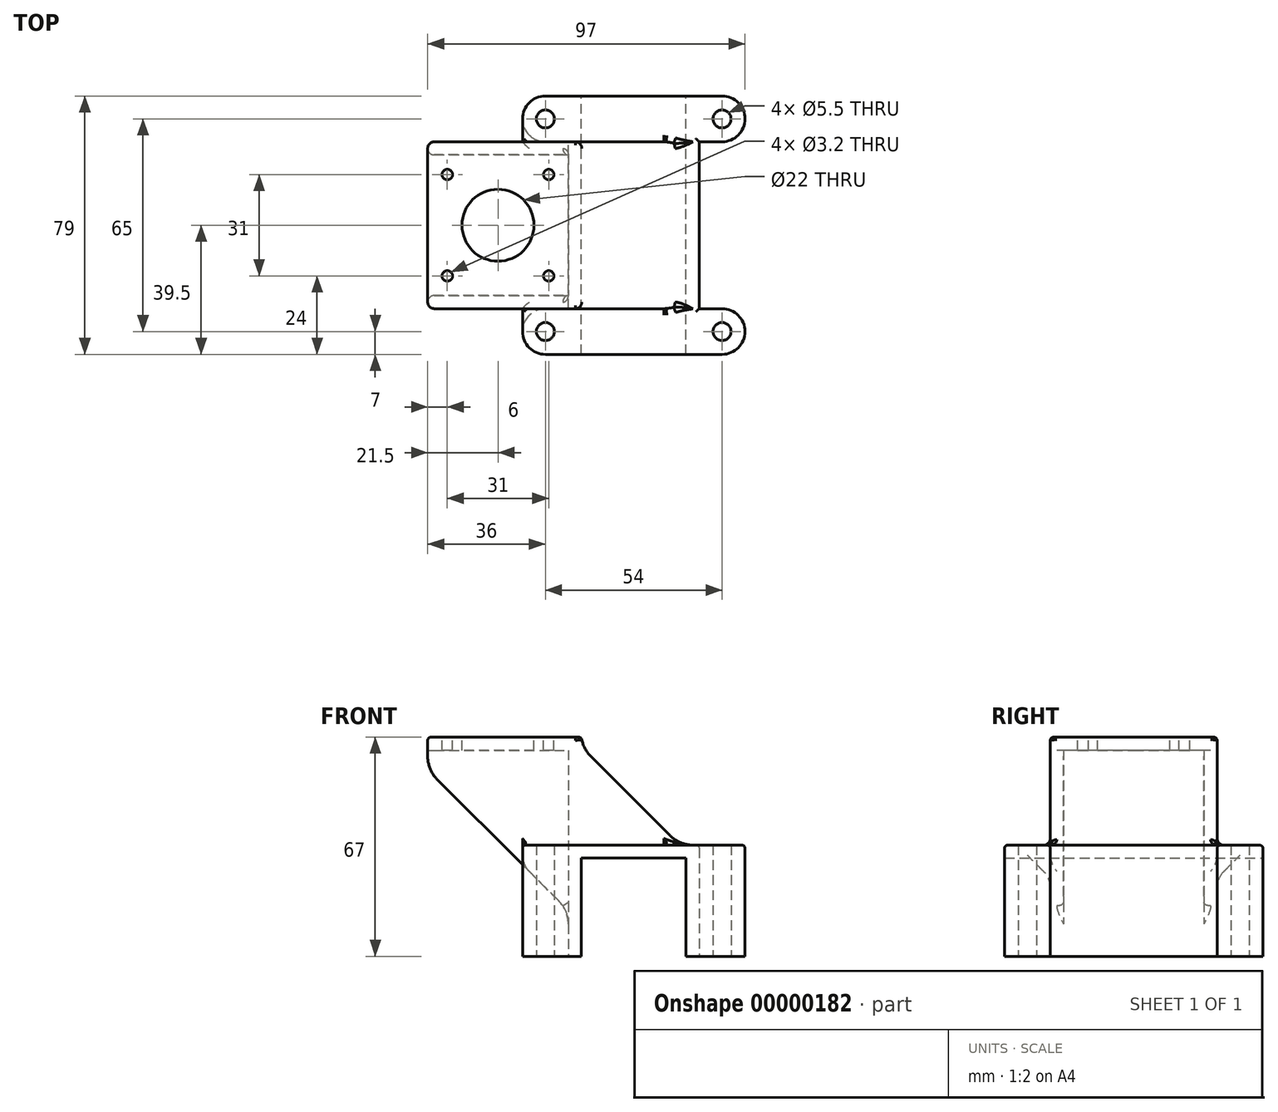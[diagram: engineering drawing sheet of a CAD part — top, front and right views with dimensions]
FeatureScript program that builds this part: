
annotation { "Feature Type Name" : "Feature", "Feature Type Description" : "" }
export const myFeature = defineFeature(function(context is Context, id is Id, definition is map)
    precondition{}
    {
        {
            var Q0;
            Q0=qCreatedBy(makeId("Front.planeOp"),FACE);
            var sketch = newSketch(context, id + "F0", { "sketchPlane" : qUnion([Q0])});
            skLineSegment(sketch, "E0.bottom", {"start": v(-20, 20) * mm, "end": v(20, 20) * mm});
            skLineSegment(sketch, "E0.top", {"start": v(-20, 0) * mm, "end": v(20, 0) * mm, "construction": true});
            skLineSegment(sketch, "E0.left", {"start": v(-20, 20) * mm, "end": v(-20, 0) * mm});
            skLineSegment(sketch, "E0.right", {"start": v(20, 20) * mm, "end": v(20, 0) * mm});
            skLineSegment(sketch, "E1.bottom", {"start": v(-16, 0) * mm, "end": v(16, 0) * mm, "construction": true});
            skLineSegment(sketch, "E1.top", {"start": v(-16, 16) * mm, "end": v(16, 16) * mm});
            skLineSegment(sketch, "E1.left", {"start": v(-16, 0) * mm, "end": v(-16, 16) * mm});
            skLineSegment(sketch, "E1.right", {"start": v(16, 0) * mm, "end": v(16, 16) * mm});
            skLineSegment(sketch, "E2", {"start": v(-20, 0) * mm, "end": v(-16, 0) * mm});
            skLineSegment(sketch, "E3", {"start": v(16, 0) * mm, "end": v(20, 0) * mm});
            skSolve(sketch);
        }
        {
            var Q0;
            Q0=makeQuery(id+"F0.imprint","IMPRINT",FACE,{"disambiguationData":[TD([[makeQuery(id+"F0.imprint","IMPRINT",EDGE,{"derivedFrom":sQuery(id+"F0.wireOp",EDGE,"E0.bottom")}),-1.0]])]});
            extrude(context, id + "F1", {"entities" : qUnion([Q0]), "depth" : 79 * mm});
        }
        {
            var Q0;
            Q0=qCreatedBy(makeId("Top.planeOp"),FACE);
            var sketch = newSketch(context, id + "F2", { "sketchPlane" : qUnion([Q0])});
            skCircle(sketch, "E4", {"center": v(-27, -7) * mm, "radius": 7 * mm, "construction": true});
            skCircle(sketch, "E5", {"center": v(-27, -72) * mm, "radius": 7 * mm, "construction": true});
            skCircle(sketch, "E6", {"center": v(27, -7) * mm, "radius": 7 * mm, "construction": true});
            skCircle(sketch, "E7", {"center": v(27, -72) * mm, "radius": 7 * mm, "construction": true});
            skLineSegment(sketch, "E8.bottom", {"start": v(-27, 0) * mm, "end": v(-20, 0) * mm});
            skLineSegment(sketch, "E8.top", {"start": v(-27, -14) * mm, "end": v(-20, -14) * mm});
            skLineSegment(sketch, "E8.left", {"start": v(-27, 0) * mm, "end": v(-27, -14) * mm});
            skLineSegment(sketch, "E8.right", {"start": v(-20, 0) * mm, "end": v(-20, -14) * mm});
            skLineSegment(sketch, "E9.bottom", {"start": v(27, 0) * mm, "end": v(20, 0) * mm});
            skLineSegment(sketch, "E9.top", {"start": v(27, -14) * mm, "end": v(20, -14) * mm});
            skLineSegment(sketch, "E9.left", {"start": v(27, 0) * mm, "end": v(27, -14) * mm});
            skLineSegment(sketch, "E9.right", {"start": v(20, 0) * mm, "end": v(20, -14) * mm});
            skLineSegment(sketch, "E10.bottom", {"start": v(-27, -65) * mm, "end": v(-20, -65) * mm});
            skLineSegment(sketch, "E10.top", {"start": v(-27, -79) * mm, "end": v(-20, -79) * mm});
            skLineSegment(sketch, "E10.left", {"start": v(-27, -65) * mm, "end": v(-27, -79) * mm});
            skLineSegment(sketch, "E10.right", {"start": v(-20, -65) * mm, "end": v(-20, -79) * mm});
            skLineSegment(sketch, "E11.bottom", {"start": v(27, -65) * mm, "end": v(20, -65) * mm});
            skLineSegment(sketch, "E11.top", {"start": v(27, -79) * mm, "end": v(20, -79) * mm});
            skLineSegment(sketch, "E11.left", {"start": v(27, -65) * mm, "end": v(27, -79) * mm});
            skLineSegment(sketch, "E11.right", {"start": v(20, -65) * mm, "end": v(20, -79) * mm});
            skLineSegment(sketch, "E12.bottom", {"start": v(-27, 0) * mm, "end": v(-34, 0) * mm});
            skLineSegment(sketch, "E12.top", {"start": v(-27, -14) * mm, "end": v(-34, -14) * mm});
            skLineSegment(sketch, "E12.right", {"start": v(-34, 0) * mm, "end": v(-34, -14) * mm});
            skLineSegment(sketch, "E13.bottom", {"start": v(-27, -65) * mm, "end": v(-34, -65) * mm});
            skLineSegment(sketch, "E13.top", {"start": v(-27, -79) * mm, "end": v(-34, -79) * mm});
            skLineSegment(sketch, "E13.right", {"start": v(-34, -65) * mm, "end": v(-34, -79) * mm});
            skLineSegment(sketch, "E14.bottom", {"start": v(27, 0) * mm, "end": v(34, 0) * mm});
            skLineSegment(sketch, "E14.top", {"start": v(27, -14) * mm, "end": v(34, -14) * mm});
            skLineSegment(sketch, "E14.right", {"start": v(34, 0) * mm, "end": v(34, -14) * mm});
            skLineSegment(sketch, "E15.bottom", {"start": v(27, -65) * mm, "end": v(34, -65) * mm});
            skLineSegment(sketch, "E15.top", {"start": v(27, -79) * mm, "end": v(34, -79) * mm});
            skLineSegment(sketch, "E15.right", {"start": v(34, -65) * mm, "end": v(34, -79) * mm});
            skSolve(sketch);
        }
        {
            var Q0;
            {Q0=qUnion([makeQuery(id+"F2.imprint","IMPRINT",FACE,{"disambiguationData":[TD([[makeQuery(id+"F2.imprint","IMPRINT",EDGE,{"derivedFrom":sQuery(id+"F2.wireOp",EDGE,"E8.bottom")}),-1.0]])]}),makeQuery(id+"F2.imprint","IMPRINT",FACE,{"disambiguationData":[TD([[makeQuery(id+"F2.imprint","IMPRINT",EDGE,{"derivedFrom":sQuery(id+"F2.wireOp",EDGE,"E12.bottom")}),1.0]])]}),makeQuery(id+"F2.imprint","IMPRINT",FACE,{"disambiguationData":[TD([[makeQuery(id+"F2.imprint","IMPRINT",EDGE,{"derivedFrom":sQuery(id+"F2.wireOp",EDGE,"E9.bottom")}),1.0]])]}),makeQuery(id+"F2.imprint","IMPRINT",FACE,{"disambiguationData":[TD([[makeQuery(id+"F2.imprint","IMPRINT",EDGE,{"derivedFrom":sQuery(id+"F2.wireOp",EDGE,"E14.bottom")}),-1.0]])]}),makeQuery(id+"F2.imprint","IMPRINT",FACE,{"disambiguationData":[TD([[makeQuery(id+"F2.imprint","IMPRINT",EDGE,{"derivedFrom":sQuery(id+"F2.wireOp",EDGE,"E10.bottom")}),-1.0]])]}),makeQuery(id+"F2.imprint","IMPRINT",FACE,{"disambiguationData":[TD([[makeQuery(id+"F2.imprint","IMPRINT",EDGE,{"derivedFrom":sQuery(id+"F2.wireOp",EDGE,"E13.bottom")}),1.0]])]}),makeQuery(id+"F2.imprint","IMPRINT",FACE,{"disambiguationData":[TD([[makeQuery(id+"F2.imprint","IMPRINT",EDGE,{"derivedFrom":sQuery(id+"F2.wireOp",EDGE,"E11.bottom")}),1.0]])]}),makeQuery(id+"F2.imprint","IMPRINT",FACE,{"disambiguationData":[TD([[makeQuery(id+"F2.imprint","IMPRINT",EDGE,{"derivedFrom":sQuery(id+"F2.wireOp",EDGE,"E15.bottom")}),-1.0]])]})]);}
            var Q1;
            Q1=makeQuery(id+"F1.opExtrude","SWEPT_FACE",FACE,{"disambiguationData":[OSD([sQuery(id+"F0.wireOp",EDGE,"E0.bottom")])]});
            extrude(context, id + "F3", {"entities" : qUnion([Q0]), "operationType" : NewBodyOperationType.ADD, "endBound" : BoundingType.UP_TO_SURFACE, "endBoundEntityFace" : qUnion([Q1]), "depth" : 25 * mm});
        }
        {
            var Q0;
            Q0=qCreatedBy(makeId("Top.planeOp"),FACE);
            var sketch = newSketch(context, id + "F4", { "sketchPlane" : qUnion([Q0])});
            skCircle(sketch, "E16", {"center": v(-27, -7) * mm, "radius": 2.75 * mm});
            skCircle(sketch, "E17", {"center": v(27, -7) * mm, "radius": 2.75 * mm});
            skCircle(sketch, "E18", {"center": v(27, -72) * mm, "radius": 2.75 * mm});
            skCircle(sketch, "E19", {"center": v(-27, -72) * mm, "radius": 2.75 * mm});
            skLineSegment(sketch, "E20.bottom", {"start": v(-27, -7) * mm, "end": v(27, -7) * mm, "construction": true});
            skLineSegment(sketch, "E20.top", {"start": v(-27, -72) * mm, "end": v(27, -72) * mm, "construction": true});
            skLineSegment(sketch, "E20.left", {"start": v(-27, -7) * mm, "end": v(-27, -72) * mm, "construction": true});
            skLineSegment(sketch, "E20.right", {"start": v(27, -7) * mm, "end": v(27, -72) * mm, "construction": true});
            skSolve(sketch);
        }
        {
            var Q0;
            {Q0=qUnion([makeQuery(id+"F4.imprint","IMPRINT",FACE,{"disambiguationData":[TD([[makeQuery(id+"F4.imprint","IMPRINT",EDGE,{"derivedFrom":sQuery(id+"F4.wireOp",EDGE,"E16")}),1.0]])]}),makeQuery(id+"F4.imprint","IMPRINT",FACE,{"disambiguationData":[TD([[makeQuery(id+"F4.imprint","IMPRINT",EDGE,{"derivedFrom":sQuery(id+"F4.wireOp",EDGE,"E17")}),1.0]])]}),makeQuery(id+"F4.imprint","IMPRINT",FACE,{"disambiguationData":[TD([[makeQuery(id+"F4.imprint","IMPRINT",EDGE,{"derivedFrom":sQuery(id+"F4.wireOp",EDGE,"E18")}),1.0]])]}),makeQuery(id+"F4.imprint","IMPRINT",FACE,{"disambiguationData":[TD([[makeQuery(id+"F4.imprint","IMPRINT",EDGE,{"derivedFrom":sQuery(id+"F4.wireOp",EDGE,"E19")}),1.0]])]})]);}
            var Q1;
            Q1=makeQuery(id+"F3.boolean.opBoolean","MERGE",FACE,{"derivedFrom":[makeQuery(id+"F1.opExtrude","SWEPT_FACE",FACE,{"disambiguationData":[OSD([sQuery(id+"F0.wireOp",EDGE,"E0.bottom")])]}),makeQuery(id+"F3.opExtrude","CAP_FACE",FACE,{"disambiguationData":[OSD([sQuery(id+"F2.wireOp",EDGE,"E8.bottom"),sQuery(id+"F2.wireOp",EDGE,"E8.top"),sQuery(id+"F2.wireOp",EDGE,"E8.right"),sQuery(id+"F2.wireOp",EDGE,"E12.bottom"),sQuery(id+"F2.wireOp",EDGE,"E12.top"),sQuery(id+"F2.wireOp",EDGE,"E12.right")])],"isStart":false}),makeQuery(id+"F3.opExtrude","CAP_FACE",FACE,{"disambiguationData":[OSD([sQuery(id+"F2.wireOp",EDGE,"E9.bottom"),sQuery(id+"F2.wireOp",EDGE,"E9.top"),sQuery(id+"F2.wireOp",EDGE,"E9.right"),sQuery(id+"F2.wireOp",EDGE,"E14.bottom"),sQuery(id+"F2.wireOp",EDGE,"E14.top"),sQuery(id+"F2.wireOp",EDGE,"E14.right")])],"isStart":false}),makeQuery(id+"F3.opExtrude","CAP_FACE",FACE,{"disambiguationData":[OSD([sQuery(id+"F2.wireOp",EDGE,"E10.bottom"),sQuery(id+"F2.wireOp",EDGE,"E10.top"),sQuery(id+"F2.wireOp",EDGE,"E10.right"),sQuery(id+"F2.wireOp",EDGE,"E13.bottom"),sQuery(id+"F2.wireOp",EDGE,"E13.top"),sQuery(id+"F2.wireOp",EDGE,"E13.right")])],"isStart":false}),makeQuery(id+"F3.opExtrude","CAP_FACE",FACE,{"disambiguationData":[OSD([sQuery(id+"F2.wireOp",EDGE,"E11.bottom"),sQuery(id+"F2.wireOp",EDGE,"E11.top"),sQuery(id+"F2.wireOp",EDGE,"E11.right"),sQuery(id+"F2.wireOp",EDGE,"E15.bottom"),sQuery(id+"F2.wireOp",EDGE,"E15.top"),sQuery(id+"F2.wireOp",EDGE,"E15.right")])],"isStart":false})]});
            extrude(context, id + "F5", {"entities" : qUnion([Q0]), "operationType" : NewBodyOperationType.REMOVE, "endBound" : BoundingType.UP_TO_SURFACE, "endBoundEntityFace" : qUnion([Q1]), "depth" : 25 * mm});
        }
        {
            var Q0;
            Q0=makeQuery(id+"F3.boolean.opBoolean","MERGE",FACE,{"derivedFrom":[makeQuery(id+"F1.opExtrude","SWEPT_FACE",FACE,{"disambiguationData":[OSD([sQuery(id+"F0.wireOp",EDGE,"E2")])]}),makeQuery(id+"F3.opExtrude","CAP_FACE",FACE,{"disambiguationData":[OSD([sQuery(id+"F2.wireOp",EDGE,"E8.bottom"),sQuery(id+"F2.wireOp",EDGE,"E8.top"),sQuery(id+"F2.wireOp",EDGE,"E8.right"),sQuery(id+"F2.wireOp",EDGE,"E12.bottom"),sQuery(id+"F2.wireOp",EDGE,"E12.top"),sQuery(id+"F2.wireOp",EDGE,"E12.right")])],"isStart":true}),makeQuery(id+"F3.opExtrude","CAP_FACE",FACE,{"disambiguationData":[OSD([sQuery(id+"F2.wireOp",EDGE,"E10.bottom"),sQuery(id+"F2.wireOp",EDGE,"E10.top"),sQuery(id+"F2.wireOp",EDGE,"E10.right"),sQuery(id+"F2.wireOp",EDGE,"E13.bottom"),sQuery(id+"F2.wireOp",EDGE,"E13.top"),sQuery(id+"F2.wireOp",EDGE,"E13.right")])],"isStart":true})]});
            var Q1;
            Q1=makeQuery(id+"F3.boolean.opBoolean","MERGE",FACE,{"derivedFrom":[makeQuery(id+"F1.opExtrude","SWEPT_FACE",FACE,{"disambiguationData":[OSD([sQuery(id+"F0.wireOp",EDGE,"E3")])]}),makeQuery(id+"F3.opExtrude","CAP_FACE",FACE,{"disambiguationData":[OSD([sQuery(id+"F2.wireOp",EDGE,"E9.bottom"),sQuery(id+"F2.wireOp",EDGE,"E9.top"),sQuery(id+"F2.wireOp",EDGE,"E9.right"),sQuery(id+"F2.wireOp",EDGE,"E14.bottom"),sQuery(id+"F2.wireOp",EDGE,"E14.top"),sQuery(id+"F2.wireOp",EDGE,"E14.right")])],"isStart":true}),makeQuery(id+"F3.opExtrude","CAP_FACE",FACE,{"disambiguationData":[OSD([sQuery(id+"F2.wireOp",EDGE,"E11.bottom"),sQuery(id+"F2.wireOp",EDGE,"E11.top"),sQuery(id+"F2.wireOp",EDGE,"E11.right"),sQuery(id+"F2.wireOp",EDGE,"E15.bottom"),sQuery(id+"F2.wireOp",EDGE,"E15.top"),sQuery(id+"F2.wireOp",EDGE,"E15.right")])],"isStart":true})]});
            extrude(context, id + "F6", {"entities" : qUnion([Q0, Q1]), "operationType" : NewBodyOperationType.ADD, "depth" : 14 * mm});
        }
        {
            var Q0;
            Q0=qCreatedBy(makeId("Top.planeOp"),FACE);
            var sketch = newSketch(context, id + "F7", { "sketchPlane" : qUnion([Q0])});
            skLineSegment(sketch, "E21.bottom", {"start": v(-63, -14) * mm, "end": v(-16, -14) * mm});
            skLineSegment(sketch, "E21.top", {"start": v(-63, -65) * mm, "end": v(-16, -65) * mm});
            skLineSegment(sketch, "E21.left", {"start": v(-63, -14) * mm, "end": v(-63, -65) * mm});
            skLineSegment(sketch, "E21.right", {"start": v(-16, -14) * mm, "end": v(-16, -65) * mm});
            skLineSegment(sketch, "E22", {"start": v(-63, -39.5) * mm, "end": v(20, -39.5) * mm, "construction": true});
            skSolve(sketch);
        }
        {
            var Q0;
            Q0=makeQuery(id+"F7.imprint","IMPRINT",FACE,{"disambiguationData":[TD([[makeQuery(id+"F7.imprint","IMPRINT",EDGE,{"derivedFrom":sQuery(id+"F7.wireOp",EDGE,"E21.bottom")}),-1.0]])]});
            var Q1;
            Q1=makeQuery(id+"F1.opExtrude","SWEPT_FACE",FACE,{"disambiguationData":[OSD([sQuery(id+"F0.wireOp",EDGE,"E1.top")])]});
            extrude(context, id + "F8", {"entities" : qUnion([Q0]), "operationType" : NewBodyOperationType.ADD, "endBoundEntity" : qUnion([Q1]), "depth" : 53 * mm});
        }
        {
            var Q0;
            Q0=makeQuery(id+"F8.opExtrude","CAP_EDGE",EDGE,{"disambiguationData":[OSD([sQuery(id+"F7.wireOp",EDGE,"E21.left")])],"isStart":true});
            chamfer(context, id + "F9", {"entities" : qUnion([Q0]), "width" : 43 * mm, "tangentPropagation" : true});
        }
        {
            var Q0;
            Q0=qCreatedBy(makeId("Top.planeOp"),FACE);
            var sketch = newSketch(context, id + "F10", { "sketchPlane" : qUnion([Q0])});
            skLineSegment(sketch, "E23.bottom", {"start": v(-63, -18) * mm, "end": v(-20, -18) * mm});
            skLineSegment(sketch, "E23.top", {"start": v(-63, -61) * mm, "end": v(-20, -61) * mm});
            skLineSegment(sketch, "E23.left", {"start": v(-63, -18) * mm, "end": v(-63, -61) * mm});
            skLineSegment(sketch, "E23.right", {"start": v(-20, -18) * mm, "end": v(-20, -61) * mm});
            skLineSegment(sketch, "E24", {"start": v(-63, -39.5) * mm, "end": v(-20, -39.5) * mm, "construction": true});
            skSolve(sketch);
        }
        {
            var Q0;
            Q0=makeQuery(id+"F10.imprint","IMPRINT",FACE,{"disambiguationData":[TD([[makeQuery(id+"F10.imprint","IMPRINT",EDGE,{"derivedFrom":sQuery(id+"F10.wireOp",EDGE,"E23.bottom")}),-1.0]])]});
            extrude(context, id + "F11", {"entities" : qUnion([Q0]), "operationType" : NewBodyOperationType.REMOVE, "depth" : 49 * mm});
        }
        {
            var Q0;
            Q0=makeQuery(id+"F8.boolean.opBoolean","INTERSECT",EDGE,{"derivedFrom":[makeQuery(id+"F3.boolean.opBoolean","MERGE",FACE,{"derivedFrom":[makeQuery(id+"F1.opExtrude","SWEPT_FACE",FACE,{"disambiguationData":[OSD([sQuery(id+"F0.wireOp",EDGE,"E0.bottom")])]}),makeQuery(id+"F3.opExtrude","CAP_FACE",FACE,{"disambiguationData":[OSD([sQuery(id+"F2.wireOp",EDGE,"E8.bottom"),sQuery(id+"F2.wireOp",EDGE,"E8.top"),sQuery(id+"F2.wireOp",EDGE,"E8.right"),sQuery(id+"F2.wireOp",EDGE,"E12.bottom"),sQuery(id+"F2.wireOp",EDGE,"E12.top"),sQuery(id+"F2.wireOp",EDGE,"E12.right")])],"isStart":false}),makeQuery(id+"F3.opExtrude","CAP_FACE",FACE,{"disambiguationData":[OSD([sQuery(id+"F2.wireOp",EDGE,"E9.bottom"),sQuery(id+"F2.wireOp",EDGE,"E9.top"),sQuery(id+"F2.wireOp",EDGE,"E9.right"),sQuery(id+"F2.wireOp",EDGE,"E14.bottom"),sQuery(id+"F2.wireOp",EDGE,"E14.top"),sQuery(id+"F2.wireOp",EDGE,"E14.right")])],"isStart":false}),makeQuery(id+"F3.opExtrude","CAP_FACE",FACE,{"disambiguationData":[OSD([sQuery(id+"F2.wireOp",EDGE,"E10.bottom"),sQuery(id+"F2.wireOp",EDGE,"E10.top"),sQuery(id+"F2.wireOp",EDGE,"E10.right"),sQuery(id+"F2.wireOp",EDGE,"E13.bottom"),sQuery(id+"F2.wireOp",EDGE,"E13.top"),sQuery(id+"F2.wireOp",EDGE,"E13.right")])],"isStart":false}),makeQuery(id+"F3.opExtrude","CAP_FACE",FACE,{"disambiguationData":[OSD([sQuery(id+"F2.wireOp",EDGE,"E11.bottom"),sQuery(id+"F2.wireOp",EDGE,"E11.top"),sQuery(id+"F2.wireOp",EDGE,"E11.right"),sQuery(id+"F2.wireOp",EDGE,"E15.bottom"),sQuery(id+"F2.wireOp",EDGE,"E15.top"),sQuery(id+"F2.wireOp",EDGE,"E15.right")])],"isStart":false})]}),makeQuery(id+"F8.opExtrude","SWEPT_FACE",FACE,{"disambiguationData":[OSD([sQuery(id+"F7.wireOp",EDGE,"E21.right")])]})]});
            chamfer(context, id + "F12", {"entities" : qUnion([Q0]), "width" : 30 * mm, "tangentPropagation" : true});
        }
        {
            var Q0;
            {var subQ0=makeQuery(id+"F3.boolean.opBoolean","MERGE",FACE,{"derivedFrom":[makeQuery(id+"F1.opExtrude","SWEPT_FACE",FACE,{"disambiguationData":[OSD([sQuery(id+"F0.wireOp",EDGE,"E0.bottom")])]}),makeQuery(id+"F3.opExtrude","CAP_FACE",FACE,{"disambiguationData":[OSD([sQuery(id+"F2.wireOp",EDGE,"E8.bottom"),sQuery(id+"F2.wireOp",EDGE,"E8.top"),sQuery(id+"F2.wireOp",EDGE,"E8.right"),sQuery(id+"F2.wireOp",EDGE,"E12.bottom"),sQuery(id+"F2.wireOp",EDGE,"E12.top"),sQuery(id+"F2.wireOp",EDGE,"E12.right")])],"isStart":false}),makeQuery(id+"F3.opExtrude","CAP_FACE",FACE,{"disambiguationData":[OSD([sQuery(id+"F2.wireOp",EDGE,"E9.bottom"),sQuery(id+"F2.wireOp",EDGE,"E9.top"),sQuery(id+"F2.wireOp",EDGE,"E9.right"),sQuery(id+"F2.wireOp",EDGE,"E14.bottom"),sQuery(id+"F2.wireOp",EDGE,"E14.top"),sQuery(id+"F2.wireOp",EDGE,"E14.right")])],"isStart":false}),makeQuery(id+"F3.opExtrude","CAP_FACE",FACE,{"disambiguationData":[OSD([sQuery(id+"F2.wireOp",EDGE,"E10.bottom"),sQuery(id+"F2.wireOp",EDGE,"E10.top"),sQuery(id+"F2.wireOp",EDGE,"E10.right"),sQuery(id+"F2.wireOp",EDGE,"E13.bottom"),sQuery(id+"F2.wireOp",EDGE,"E13.top"),sQuery(id+"F2.wireOp",EDGE,"E13.right")])],"isStart":false}),makeQuery(id+"F3.opExtrude","CAP_FACE",FACE,{"disambiguationData":[OSD([sQuery(id+"F2.wireOp",EDGE,"E11.bottom"),sQuery(id+"F2.wireOp",EDGE,"E11.top"),sQuery(id+"F2.wireOp",EDGE,"E11.right"),sQuery(id+"F2.wireOp",EDGE,"E15.bottom"),sQuery(id+"F2.wireOp",EDGE,"E15.top"),sQuery(id+"F2.wireOp",EDGE,"E15.right")])],"isStart":false})]});Q0=makeQuery(id+"F12.opChamfer","BLEND_EDGE",EDGE,{"blendedFrom":[makeQuery(id+"F8.boolean.opBoolean","INTERSECT",EDGE,{"derivedFrom":[subQ0,makeQuery(id+"F8.opExtrude","SWEPT_FACE",FACE,{"disambiguationData":[OSD([sQuery(id+"F7.wireOp",EDGE,"E21.right")])]})]}),subQ0],"blendedInto":[subQ0]});}
            var Q1;
            {var subQ0=makeQuery(id+"F8.opExtrude","SWEPT_FACE",FACE,{"disambiguationData":[OSD([sQuery(id+"F7.wireOp",EDGE,"E21.right")])]});Q1=makeQuery(id+"F12.opChamfer","BLEND_EDGE",EDGE,{"blendedFrom":[makeQuery(id+"F8.boolean.opBoolean","INTERSECT",EDGE,{"derivedFrom":[makeQuery(id+"F3.boolean.opBoolean","MERGE",FACE,{"derivedFrom":[makeQuery(id+"F1.opExtrude","SWEPT_FACE",FACE,{"disambiguationData":[OSD([sQuery(id+"F0.wireOp",EDGE,"E0.bottom")])]}),makeQuery(id+"F3.opExtrude","CAP_FACE",FACE,{"disambiguationData":[OSD([sQuery(id+"F2.wireOp",EDGE,"E8.bottom"),sQuery(id+"F2.wireOp",EDGE,"E8.top"),sQuery(id+"F2.wireOp",EDGE,"E8.right"),sQuery(id+"F2.wireOp",EDGE,"E12.bottom"),sQuery(id+"F2.wireOp",EDGE,"E12.top"),sQuery(id+"F2.wireOp",EDGE,"E12.right")])],"isStart":false}),makeQuery(id+"F3.opExtrude","CAP_FACE",FACE,{"disambiguationData":[OSD([sQuery(id+"F2.wireOp",EDGE,"E9.bottom"),sQuery(id+"F2.wireOp",EDGE,"E9.top"),sQuery(id+"F2.wireOp",EDGE,"E9.right"),sQuery(id+"F2.wireOp",EDGE,"E14.bottom"),sQuery(id+"F2.wireOp",EDGE,"E14.top"),sQuery(id+"F2.wireOp",EDGE,"E14.right")])],"isStart":false}),makeQuery(id+"F3.opExtrude","CAP_FACE",FACE,{"disambiguationData":[OSD([sQuery(id+"F2.wireOp",EDGE,"E10.bottom"),sQuery(id+"F2.wireOp",EDGE,"E10.top"),sQuery(id+"F2.wireOp",EDGE,"E10.right"),sQuery(id+"F2.wireOp",EDGE,"E13.bottom"),sQuery(id+"F2.wireOp",EDGE,"E13.top"),sQuery(id+"F2.wireOp",EDGE,"E13.right")])],"isStart":false}),makeQuery(id+"F3.opExtrude","CAP_FACE",FACE,{"disambiguationData":[OSD([sQuery(id+"F2.wireOp",EDGE,"E11.bottom"),sQuery(id+"F2.wireOp",EDGE,"E11.top"),sQuery(id+"F2.wireOp",EDGE,"E11.right"),sQuery(id+"F2.wireOp",EDGE,"E15.bottom"),sQuery(id+"F2.wireOp",EDGE,"E15.top"),sQuery(id+"F2.wireOp",EDGE,"E15.right")])],"isStart":false})]}),subQ0]}),subQ0],"blendedInto":[subQ0]});}
            var Q2;
            {var subQ0=sQuery(id+"F7.wireOp",EDGE,"E21.left");var subQ1=makeQuery(id+"F8.opExtrude","SWEPT_FACE",FACE,{"disambiguationData":[OSD([subQ0])]});Q2=makeQuery(id+"F11.boolean.opBoolean","SPLIT",EDGE,{"disambiguationData":[TD([makeQuery(id+"F8.opExtrude","SWEPT_FACE",FACE,{"disambiguationData":[OSD([sQuery(id+"F7.wireOp",EDGE,"E21.bottom")])]})])],"derivedFrom":makeQuery(id+"F9.opChamfer","BLEND_EDGE",EDGE,{"blendedFrom":[makeQuery(id+"F8.opExtrude","CAP_EDGE",EDGE,{"disambiguationData":[OSD([subQ0])],"isStart":true}),subQ1],"blendedInto":[subQ1]})});}
            var Q3;
            {var subQ0=sQuery(id+"F7.wireOp",EDGE,"E21.left");var subQ1=makeQuery(id+"F8.opExtrude","SWEPT_FACE",FACE,{"disambiguationData":[OSD([subQ0])]});Q3=makeQuery(id+"F11.boolean.opBoolean","SPLIT",EDGE,{"disambiguationData":[TD([makeQuery(id+"F8.opExtrude","SWEPT_FACE",FACE,{"disambiguationData":[OSD([sQuery(id+"F7.wireOp",EDGE,"E21.top")])]})])],"derivedFrom":makeQuery(id+"F9.opChamfer","BLEND_EDGE",EDGE,{"blendedFrom":[makeQuery(id+"F8.opExtrude","CAP_EDGE",EDGE,{"disambiguationData":[OSD([subQ0])],"isStart":true}),subQ1],"blendedInto":[subQ1]})});}
            var Q4;
            {var subQ0=sQuery(id+"F7.imprint",EDGE,"E21.left");var subQ1=makeQuery(id+"F1.opExtrude","SWEPT_FACE",FACE,{"disambiguationData":[OSD([sQuery(id+"F0.imprint",EDGE,"E2")])]});var subQ2=sQuery(id+"F2.imprint",EDGE,"E8.left");var subQ3=sQuery(id+"F2.imprint",VERTEX,"E8.bottom.start");var subQ5=makeQuery(id+"F2.imprint","SKETCH_ENTITY",EDGE,{"disambiguationData":[TD([[subQ3,-1.0]])],"sketchEntityId":"E4"});var subQ9=makeQuery(id+"F3.opExtrude","CAP_FACE",FACE,{"disambiguationData":[OSD([makeQuery(id+"F2.imprint","IMPRINT",FACE,{"disambiguationData":[TD([[subQ2,-1.0]])]})])],"isStart":true});var subQ10=sQuery(id+"F2.imprint",EDGE,"E10.left");var subQ16=makeQuery(id+"F3.opExtrude","CAP_FACE",FACE,{"disambiguationData":[OSD([makeQuery(id+"F2.imprint","IMPRINT",FACE,{"disambiguationData":[TD([[subQ10,-1.0]])]})])],"isStart":true});var subQ17=sQuery(id+"F7.imprint",EDGE,"E21.bottom");var subQ18=makeQuery(id+"F8.opExtrude","CAP_FACE",FACE,{"disambiguationData":[OSD([makeQuery(id+"F7.imprint","IMPRINT",FACE,{"disambiguationData":[TD([[subQ17,-1.0]])]})])],"isStart":true});Q4=makeQuery(id+"F11.boolean.opBoolean","SPLIT",EDGE,{"disambiguationData":[TD([makeQuery(id+"F3.opExtrude","SWEPT_FACE",FACE,{"disambiguationData":[OSD([subQ5])]})])],"derivedFrom":makeQuery(id+"F9.opChamfer","BLEND_EDGE",EDGE,{"blendedFrom":[makeQuery(id+"F8.opExtrude","CAP_EDGE",EDGE,{"disambiguationData":[OSD([subQ0])],"isStart":true}),makeQuery(id+"F8.boolean.opBoolean","MERGE",FACE,{"derivedFrom":[makeQuery(id+"F3.boolean.opBoolean","MERGE",FACE,{"derivedFrom":[subQ1,subQ9,subQ16]}),subQ18]})],"blendedInto":[makeQuery(id+"F8.boolean.opBoolean","MERGE",FACE,{"derivedFrom":[makeQuery(id+"F3.boolean.opBoolean","MERGE",FACE,{"derivedFrom":[subQ1,subQ9,subQ16]}),subQ18]})]})});}
            var Q5;
            {var subQ0=sQuery(id+"F7.imprint",EDGE,"E21.left");var subQ1=makeQuery(id+"F1.opExtrude","SWEPT_FACE",FACE,{"disambiguationData":[OSD([sQuery(id+"F0.imprint",EDGE,"E2")])]});var subQ2=sQuery(id+"F2.imprint",EDGE,"E8.left");var subQ8=makeQuery(id+"F3.opExtrude","CAP_FACE",FACE,{"disambiguationData":[OSD([makeQuery(id+"F2.imprint","IMPRINT",FACE,{"disambiguationData":[TD([[subQ2,-1.0]])]})])],"isStart":true});var subQ9=sQuery(id+"F2.imprint",EDGE,"E10.left");var subQ10=sQuery(id+"F2.imprint",VERTEX,"E10.bottom.start");var subQ12=makeQuery(id+"F2.imprint","SKETCH_ENTITY",EDGE,{"disambiguationData":[TD([[subQ10,-1.0]])],"sketchEntityId":"E5"});var subQ16=makeQuery(id+"F3.opExtrude","CAP_FACE",FACE,{"disambiguationData":[OSD([makeQuery(id+"F2.imprint","IMPRINT",FACE,{"disambiguationData":[TD([[subQ9,-1.0]])]})])],"isStart":true});var subQ18=makeQuery(id+"F8.opExtrude","CAP_FACE",FACE,{"disambiguationData":[OSD([makeQuery(id+"F7.imprint","IMPRINT",FACE,{"disambiguationData":[TD([[sQuery(id+"F7.imprint",EDGE,"E21.bottom"),-1.0]])]})])],"isStart":true});Q5=makeQuery(id+"F11.boolean.opBoolean","SPLIT",EDGE,{"disambiguationData":[TD([makeQuery(id+"F3.opExtrude","SWEPT_FACE",FACE,{"disambiguationData":[OSD([subQ12])]})])],"derivedFrom":makeQuery(id+"F9.opChamfer","BLEND_EDGE",EDGE,{"blendedFrom":[makeQuery(id+"F8.opExtrude","CAP_EDGE",EDGE,{"disambiguationData":[OSD([subQ0])],"isStart":true}),makeQuery(id+"F8.boolean.opBoolean","MERGE",FACE,{"derivedFrom":[makeQuery(id+"F3.boolean.opBoolean","MERGE",FACE,{"derivedFrom":[subQ1,subQ8,subQ16]}),subQ18]})],"blendedInto":[makeQuery(id+"F8.boolean.opBoolean","MERGE",FACE,{"derivedFrom":[makeQuery(id+"F3.boolean.opBoolean","MERGE",FACE,{"derivedFrom":[subQ1,subQ8,subQ16]}),subQ18]})]})});}
            var Q6;
            {var subQ0=sQuery(id+"F7.wireOp",EDGE,"E21.left");var subQ1=sQuery(id+"F0.wireOp",EDGE,"E0.left");var subQ2=makeQuery(id+"F1.opExtrude","SWEPT_FACE",FACE,{"disambiguationData":[OSD([subQ1])]});var subQ3=makeQuery(id+"F6.opExtrude","SWEPT_FACE",FACE,{"disambiguationData":[OSD([subQ1,sQuery(id+"F0.wireOp",EDGE,"E2")])]});Q6=makeQuery(id+"F11.boolean.opBoolean","SPLIT",EDGE,{"disambiguationData":[TD([makeQuery(id+"F11.opExtrude","SWEPT_FACE",FACE,{"disambiguationData":[OSD([sQuery(id+"F10.wireOp",EDGE,"E23.bottom")])]})])],"derivedFrom":makeQuery(id+"F9.opChamfer","BLEND_EDGE",EDGE,{"blendedFrom":[makeQuery(id+"F8.opExtrude","CAP_EDGE",EDGE,{"disambiguationData":[OSD([subQ0])],"isStart":true}),makeQuery(id+"F6.boolean.opBoolean","MERGE",FACE,{"derivedFrom":[subQ2,subQ3]})],"blendedInto":[makeQuery(id+"F6.boolean.opBoolean","MERGE",FACE,{"derivedFrom":[subQ2,subQ3]})]})});}
            var Q7;
            {var subQ0=sQuery(id+"F7.wireOp",EDGE,"E21.left");var subQ1=sQuery(id+"F0.wireOp",EDGE,"E0.left");var subQ2=makeQuery(id+"F1.opExtrude","SWEPT_FACE",FACE,{"disambiguationData":[OSD([subQ1])]});var subQ3=makeQuery(id+"F6.opExtrude","SWEPT_FACE",FACE,{"disambiguationData":[OSD([subQ1,sQuery(id+"F0.wireOp",EDGE,"E2")])]});Q7=makeQuery(id+"F11.boolean.opBoolean","SPLIT",EDGE,{"disambiguationData":[TD([makeQuery(id+"F11.opExtrude","SWEPT_FACE",FACE,{"disambiguationData":[OSD([sQuery(id+"F10.wireOp",EDGE,"E23.top")])]})])],"derivedFrom":makeQuery(id+"F9.opChamfer","BLEND_EDGE",EDGE,{"blendedFrom":[makeQuery(id+"F8.opExtrude","CAP_EDGE",EDGE,{"disambiguationData":[OSD([subQ0])],"isStart":true}),makeQuery(id+"F6.boolean.opBoolean","MERGE",FACE,{"derivedFrom":[subQ2,subQ3]})],"blendedInto":[makeQuery(id+"F6.boolean.opBoolean","MERGE",FACE,{"derivedFrom":[subQ2,subQ3]})]})});}
            fillet(context, id + "F13", {"entities" : qUnion([Q0, Q1, Q2, Q3, Q4, Q5, Q6, Q7]), "radius" : 10 * mm, "tangentPropagation" : true, "allowEdgeOverflow" : false});
        }
        {
            var Q0;
            Q0=makeQuery(id+"F12.opChamfer","BLEND_EDGE",EDGE,{"blendedFrom":[makeQuery(id+"F8.boolean.opBoolean","INTERSECT",EDGE,{"derivedFrom":[makeQuery(id+"F3.boolean.opBoolean","MERGE",FACE,{"derivedFrom":[makeQuery(id+"F1.opExtrude","SWEPT_FACE",FACE,{"disambiguationData":[OSD([sQuery(id+"F0.wireOp",EDGE,"E0.bottom")])]}),makeQuery(id+"F3.opExtrude","CAP_FACE",FACE,{"disambiguationData":[OSD([sQuery(id+"F2.wireOp",EDGE,"E8.bottom"),sQuery(id+"F2.wireOp",EDGE,"E8.top"),sQuery(id+"F2.wireOp",EDGE,"E8.right"),sQuery(id+"F2.wireOp",EDGE,"E12.bottom"),sQuery(id+"F2.wireOp",EDGE,"E12.top"),sQuery(id+"F2.wireOp",EDGE,"E12.right")])],"isStart":false}),makeQuery(id+"F3.opExtrude","CAP_FACE",FACE,{"disambiguationData":[OSD([sQuery(id+"F2.wireOp",EDGE,"E9.bottom"),sQuery(id+"F2.wireOp",EDGE,"E9.top"),sQuery(id+"F2.wireOp",EDGE,"E9.right"),sQuery(id+"F2.wireOp",EDGE,"E14.bottom"),sQuery(id+"F2.wireOp",EDGE,"E14.top"),sQuery(id+"F2.wireOp",EDGE,"E14.right")])],"isStart":false}),makeQuery(id+"F3.opExtrude","CAP_FACE",FACE,{"disambiguationData":[OSD([sQuery(id+"F2.wireOp",EDGE,"E10.bottom"),sQuery(id+"F2.wireOp",EDGE,"E10.top"),sQuery(id+"F2.wireOp",EDGE,"E10.right"),sQuery(id+"F2.wireOp",EDGE,"E13.bottom"),sQuery(id+"F2.wireOp",EDGE,"E13.top"),sQuery(id+"F2.wireOp",EDGE,"E13.right")])],"isStart":false}),makeQuery(id+"F3.opExtrude","CAP_FACE",FACE,{"disambiguationData":[OSD([sQuery(id+"F2.wireOp",EDGE,"E11.bottom"),sQuery(id+"F2.wireOp",EDGE,"E11.top"),sQuery(id+"F2.wireOp",EDGE,"E11.right"),sQuery(id+"F2.wireOp",EDGE,"E15.bottom"),sQuery(id+"F2.wireOp",EDGE,"E15.top"),sQuery(id+"F2.wireOp",EDGE,"E15.right")])],"isStart":false})]}),makeQuery(id+"F8.opExtrude","SWEPT_FACE",FACE,{"disambiguationData":[OSD([sQuery(id+"F7.wireOp",EDGE,"E21.right")])]})]}),makeQuery(id+"F8.opExtrude","SWEPT_FACE",FACE,{"disambiguationData":[OSD([sQuery(id+"F7.wireOp",EDGE,"E21.bottom")])]})],"blendedInto":[makeQuery(id+"F8.opExtrude","SWEPT_FACE",FACE,{"disambiguationData":[OSD([sQuery(id+"F7.wireOp",EDGE,"E21.bottom")])]})]});
            var Q1;
            Q1=makeQuery(id+"F12.opChamfer","BLEND_EDGE",EDGE,{"blendedFrom":[makeQuery(id+"F8.boolean.opBoolean","INTERSECT",EDGE,{"derivedFrom":[makeQuery(id+"F3.boolean.opBoolean","MERGE",FACE,{"derivedFrom":[makeQuery(id+"F1.opExtrude","SWEPT_FACE",FACE,{"disambiguationData":[OSD([sQuery(id+"F0.wireOp",EDGE,"E0.bottom")])]}),makeQuery(id+"F3.opExtrude","CAP_FACE",FACE,{"disambiguationData":[OSD([sQuery(id+"F2.wireOp",EDGE,"E8.bottom"),sQuery(id+"F2.wireOp",EDGE,"E8.top"),sQuery(id+"F2.wireOp",EDGE,"E8.right"),sQuery(id+"F2.wireOp",EDGE,"E12.bottom"),sQuery(id+"F2.wireOp",EDGE,"E12.top"),sQuery(id+"F2.wireOp",EDGE,"E12.right")])],"isStart":false}),makeQuery(id+"F3.opExtrude","CAP_FACE",FACE,{"disambiguationData":[OSD([sQuery(id+"F2.wireOp",EDGE,"E9.bottom"),sQuery(id+"F2.wireOp",EDGE,"E9.top"),sQuery(id+"F2.wireOp",EDGE,"E9.right"),sQuery(id+"F2.wireOp",EDGE,"E14.bottom"),sQuery(id+"F2.wireOp",EDGE,"E14.top"),sQuery(id+"F2.wireOp",EDGE,"E14.right")])],"isStart":false}),makeQuery(id+"F3.opExtrude","CAP_FACE",FACE,{"disambiguationData":[OSD([sQuery(id+"F2.wireOp",EDGE,"E10.bottom"),sQuery(id+"F2.wireOp",EDGE,"E10.top"),sQuery(id+"F2.wireOp",EDGE,"E10.right"),sQuery(id+"F2.wireOp",EDGE,"E13.bottom"),sQuery(id+"F2.wireOp",EDGE,"E13.top"),sQuery(id+"F2.wireOp",EDGE,"E13.right")])],"isStart":false}),makeQuery(id+"F3.opExtrude","CAP_FACE",FACE,{"disambiguationData":[OSD([sQuery(id+"F2.wireOp",EDGE,"E11.bottom"),sQuery(id+"F2.wireOp",EDGE,"E11.top"),sQuery(id+"F2.wireOp",EDGE,"E11.right"),sQuery(id+"F2.wireOp",EDGE,"E15.bottom"),sQuery(id+"F2.wireOp",EDGE,"E15.top"),sQuery(id+"F2.wireOp",EDGE,"E15.right")])],"isStart":false})]}),makeQuery(id+"F8.opExtrude","SWEPT_FACE",FACE,{"disambiguationData":[OSD([sQuery(id+"F7.wireOp",EDGE,"E21.right")])]})]}),makeQuery(id+"F8.opExtrude","SWEPT_FACE",FACE,{"disambiguationData":[OSD([sQuery(id+"F7.wireOp",EDGE,"E21.top")])]})],"blendedInto":[makeQuery(id+"F8.opExtrude","SWEPT_FACE",FACE,{"disambiguationData":[OSD([sQuery(id+"F7.wireOp",EDGE,"E21.top")])]})]});
            fillet(context, id + "F14", {"entities" : qUnion([Q0, Q1]), "radius" : 2 * mm, "tangentPropagation" : true, "allowEdgeOverflow" : false});
        }
        {
            var Q0;
            Q0=makeQuery(id+"F8.opExtrude","CAP_FACE",FACE,{"disambiguationData":[OSD([sQuery(id+"F7.wireOp",EDGE,"E21.bottom"),sQuery(id+"F7.wireOp",EDGE,"E21.top"),sQuery(id+"F7.wireOp",EDGE,"E21.left"),sQuery(id+"F7.wireOp",EDGE,"E21.right")])],"isStart":false});
            var sketch = newSketch(context, id + "F15", { "sketchPlane" : qUnion([Q0])});
            skCircle(sketch, "E25", {"center": v(-41.5, -39.5) * mm, "radius": 11 * mm});
            skLineSegment(sketch, "E26", {"start": v(-63, -39.5) * mm, "end": v(-26, -39.5) * mm, "construction": true});
            skLineSegment(sketch, "E27.bottom", {"start": v(-57, -24) * mm, "end": v(-26, -24) * mm, "construction": true});
            skLineSegment(sketch, "E27.top", {"start": v(-57, -55) * mm, "end": v(-26, -55) * mm, "construction": true});
            skLineSegment(sketch, "E27.left", {"start": v(-57, -24) * mm, "end": v(-57, -55) * mm, "construction": true});
            skLineSegment(sketch, "E27.right", {"start": v(-26, -24) * mm, "end": v(-26, -55) * mm, "construction": true});
            skLineSegment(sketch, "E28", {"start": v(-41.5, -39.5) * mm, "end": v(-41.5, -24) * mm});
            skCircle(sketch, "E29", {"center": v(-57, -24) * mm, "radius": 1.6 * mm});
            skCircle(sketch, "E30", {"center": v(-26, -24) * mm, "radius": 1.6 * mm});
            skCircle(sketch, "E31", {"center": v(-26, -55) * mm, "radius": 1.6 * mm});
            skCircle(sketch, "E32", {"center": v(-57, -55) * mm, "radius": 1.6 * mm});
            skSolve(sketch);
        }
        {
            var Q0;
            {var subQ1=sQuery(id+"F15.wireOp",EDGE,"E25");Q0=qUnion([makeQuery(id+"F15.imprint","IMPRINT",FACE,{"disambiguationData":[TD([[makeQuery(id+"F15.imprint","IMPRINT",EDGE,{"derivedFrom":subQ1}),1.0]])]}),makeQuery(id+"F15.imprint","IMPRINT",FACE,{"disambiguationData":[TD([[makeQuery(id+"F15.imprint","IMPRINT",EDGE,{"derivedFrom":sQuery(id+"F15.wireOp",EDGE,"E29")}),1.0]])]}),makeQuery(id+"F15.imprint","IMPRINT",FACE,{"disambiguationData":[TD([[makeQuery(id+"F15.imprint","IMPRINT",EDGE,{"derivedFrom":sQuery(id+"F15.wireOp",EDGE,"E30")}),1.0]])]}),makeQuery(id+"F15.imprint","IMPRINT",FACE,{"disambiguationData":[TD([[makeQuery(id+"F15.imprint","IMPRINT",EDGE,{"derivedFrom":sQuery(id+"F15.wireOp",EDGE,"E31")}),1.0]])]}),makeQuery(id+"F15.imprint","IMPRINT",FACE,{"disambiguationData":[TD([[makeQuery(id+"F15.imprint","IMPRINT",EDGE,{"derivedFrom":sQuery(id+"F15.wireOp",EDGE,"E32")}),1.0]])]})]);}
            extrude(context, id + "F16", {"entities" : qUnion([Q0]), "operationType" : NewBodyOperationType.REMOVE, "endBound" : BoundingType.THROUGH_ALL, "oppositeDirection" : true, "depth" : 25 * mm});
        }
        {
            var Q0;
            Q0=makeQuery(id+"F8.boolean.opBoolean","INTERSECT",EDGE,{"derivedFrom":[makeQuery(id+"F3.boolean.opBoolean","MERGE",FACE,{"derivedFrom":[makeQuery(id+"F1.opExtrude","SWEPT_FACE",FACE,{"disambiguationData":[OSD([sQuery(id+"F0.wireOp",EDGE,"E0.bottom")])]}),makeQuery(id+"F3.opExtrude","CAP_FACE",FACE,{"disambiguationData":[OSD([sQuery(id+"F2.wireOp",EDGE,"E8.bottom"),sQuery(id+"F2.wireOp",EDGE,"E8.top"),sQuery(id+"F2.wireOp",EDGE,"E8.right"),sQuery(id+"F2.wireOp",EDGE,"E12.bottom"),sQuery(id+"F2.wireOp",EDGE,"E12.top"),sQuery(id+"F2.wireOp",EDGE,"E12.right")])],"isStart":false}),makeQuery(id+"F3.opExtrude","CAP_FACE",FACE,{"disambiguationData":[OSD([sQuery(id+"F2.wireOp",EDGE,"E9.bottom"),sQuery(id+"F2.wireOp",EDGE,"E9.top"),sQuery(id+"F2.wireOp",EDGE,"E9.right"),sQuery(id+"F2.wireOp",EDGE,"E14.bottom"),sQuery(id+"F2.wireOp",EDGE,"E14.top"),sQuery(id+"F2.wireOp",EDGE,"E14.right")])],"isStart":false}),makeQuery(id+"F3.opExtrude","CAP_FACE",FACE,{"disambiguationData":[OSD([sQuery(id+"F2.wireOp",EDGE,"E10.bottom"),sQuery(id+"F2.wireOp",EDGE,"E10.top"),sQuery(id+"F2.wireOp",EDGE,"E10.right"),sQuery(id+"F2.wireOp",EDGE,"E13.bottom"),sQuery(id+"F2.wireOp",EDGE,"E13.top"),sQuery(id+"F2.wireOp",EDGE,"E13.right")])],"isStart":false}),makeQuery(id+"F3.opExtrude","CAP_FACE",FACE,{"disambiguationData":[OSD([sQuery(id+"F2.wireOp",EDGE,"E11.bottom"),sQuery(id+"F2.wireOp",EDGE,"E11.top"),sQuery(id+"F2.wireOp",EDGE,"E11.right"),sQuery(id+"F2.wireOp",EDGE,"E15.bottom"),sQuery(id+"F2.wireOp",EDGE,"E15.top"),sQuery(id+"F2.wireOp",EDGE,"E15.right")])],"isStart":false})]}),makeQuery(id+"F8.opExtrude","SWEPT_FACE",FACE,{"disambiguationData":[OSD([sQuery(id+"F7.wireOp",EDGE,"E21.top")])]})]});
            var Q1;
            Q1=makeQuery(id+"F8.boolean.opBoolean","INTERSECT",EDGE,{"derivedFrom":[makeQuery(id+"F3.boolean.opBoolean","MERGE",FACE,{"derivedFrom":[makeQuery(id+"F1.opExtrude","SWEPT_FACE",FACE,{"disambiguationData":[OSD([sQuery(id+"F0.wireOp",EDGE,"E0.bottom")])]}),makeQuery(id+"F3.opExtrude","CAP_FACE",FACE,{"disambiguationData":[OSD([sQuery(id+"F2.wireOp",EDGE,"E8.bottom"),sQuery(id+"F2.wireOp",EDGE,"E8.top"),sQuery(id+"F2.wireOp",EDGE,"E8.right"),sQuery(id+"F2.wireOp",EDGE,"E12.bottom"),sQuery(id+"F2.wireOp",EDGE,"E12.top"),sQuery(id+"F2.wireOp",EDGE,"E12.right")])],"isStart":false}),makeQuery(id+"F3.opExtrude","CAP_FACE",FACE,{"disambiguationData":[OSD([sQuery(id+"F2.wireOp",EDGE,"E9.bottom"),sQuery(id+"F2.wireOp",EDGE,"E9.top"),sQuery(id+"F2.wireOp",EDGE,"E9.right"),sQuery(id+"F2.wireOp",EDGE,"E14.bottom"),sQuery(id+"F2.wireOp",EDGE,"E14.top"),sQuery(id+"F2.wireOp",EDGE,"E14.right")])],"isStart":false}),makeQuery(id+"F3.opExtrude","CAP_FACE",FACE,{"disambiguationData":[OSD([sQuery(id+"F2.wireOp",EDGE,"E10.bottom"),sQuery(id+"F2.wireOp",EDGE,"E10.top"),sQuery(id+"F2.wireOp",EDGE,"E10.right"),sQuery(id+"F2.wireOp",EDGE,"E13.bottom"),sQuery(id+"F2.wireOp",EDGE,"E13.top"),sQuery(id+"F2.wireOp",EDGE,"E13.right")])],"isStart":false}),makeQuery(id+"F3.opExtrude","CAP_FACE",FACE,{"disambiguationData":[OSD([sQuery(id+"F2.wireOp",EDGE,"E11.bottom"),sQuery(id+"F2.wireOp",EDGE,"E11.top"),sQuery(id+"F2.wireOp",EDGE,"E11.right"),sQuery(id+"F2.wireOp",EDGE,"E15.bottom"),sQuery(id+"F2.wireOp",EDGE,"E15.top"),sQuery(id+"F2.wireOp",EDGE,"E15.right")])],"isStart":false})]}),makeQuery(id+"F8.opExtrude","SWEPT_FACE",FACE,{"disambiguationData":[OSD([sQuery(id+"F7.wireOp",EDGE,"E21.bottom")])]})]});
            fillet(context, id + "F17", {"entities" : qUnion([Q0, Q1]), "radius" : 2 * mm, "tangentPropagation" : true, "allowEdgeOverflow" : false});
        }
        {
            var Q0;
            Q0=makeQuery(id+"F8.opExtrude","SWEPT_EDGE",EDGE,{"disambiguationData":[OSD([sQuery(id+"F7.wireOp",EDGE,"E21.bottom"),sQuery(id+"F7.wireOp",EDGE,"E21.left")])]});
            var Q1;
            Q1=makeQuery(id+"F8.opExtrude","SWEPT_EDGE",EDGE,{"disambiguationData":[OSD([sQuery(id+"F7.wireOp",EDGE,"E21.top"),sQuery(id+"F7.wireOp",EDGE,"E21.left")])]});
            var Q2;
            Q2=makeQuery(id+"F11.boolean.opBoolean","INTERSECT",EDGE,{"derivedFrom":[makeQuery(id+"F9.opChamfer","BLEND_FACE",FACE,{"disambiguationData":[OSD([sQuery(id+"F7.wireOp",EDGE,"E21.left")])]}),makeQuery(id+"F11.opExtrude","SWEPT_FACE",FACE,{"disambiguationData":[OSD([sQuery(id+"F10.wireOp",EDGE,"E23.bottom")])]})]});
            var Q3;
            Q3=makeQuery(id+"F11.boolean.opBoolean","INTERSECT",EDGE,{"derivedFrom":[makeQuery(id+"F9.opChamfer","BLEND_FACE",FACE,{"disambiguationData":[OSD([sQuery(id+"F7.wireOp",EDGE,"E21.left")])]}),makeQuery(id+"F11.opExtrude","SWEPT_FACE",FACE,{"disambiguationData":[OSD([sQuery(id+"F10.wireOp",EDGE,"E23.top")])]})]});
            fillet(context, id + "F18", {"entities" : qUnion([Q0, Q1, Q2, Q3]), "radius" : 2 * mm, "tangentPropagation" : true, "allowEdgeOverflow" : false});
        }
        {
            var Q0;
            {var subQ0=sQuery(id+"F2.wireOp",EDGE,"E13.bottom");var subQ1=sQuery(id+"F2.wireOp",EDGE,"E13.right");var subQ2=makeQuery(id+"F6.boolean.opBoolean","MERGE",EDGE,{"derivedFrom":[makeQuery(id+"F3.opExtrude","SWEPT_EDGE",EDGE,{"disambiguationData":[OSD([subQ0,subQ1])]}),makeQuery(id+"F6.opExtrude","SWEPT_EDGE",EDGE,{"disambiguationData":[OSD([subQ0,subQ1])]})]});var subQ6=sQuery(id+"F2.wireOp",EDGE,"E8.bottom");var subQ7=sQuery(id+"F2.wireOp",EDGE,"E8.top");var subQ8=sQuery(id+"F2.wireOp",EDGE,"E8.right");var subQ9=sQuery(id+"F2.wireOp",EDGE,"E10.bottom");var subQ10=sQuery(id+"F2.wireOp",EDGE,"E10.top");var subQ11=sQuery(id+"F2.wireOp",EDGE,"E10.right");var subQ12=sQuery(id+"F2.wireOp",EDGE,"E12.bottom");var subQ13=sQuery(id+"F2.wireOp",EDGE,"E12.top");var subQ14=sQuery(id+"F2.wireOp",EDGE,"E12.right");var subQ15=sQuery(id+"F2.wireOp",EDGE,"E13.top");Q0=makeQuery(id+"F9.opChamfer","MERGE",EDGE,{"derivedFrom":[makeQuery(id+"F8.boolean.opBoolean","SPLIT",EDGE,{"disambiguationData":[TD([makeQuery(id+"F6.opExtrude","CAP_FACE",FACE,{"disambiguationData":[OSD([sQuery(id+"F0.wireOp",EDGE,"E2"),subQ6,subQ7,subQ8,subQ9,subQ10,subQ11,subQ12,subQ13,subQ14,subQ0,subQ15,subQ1])],"isStart":false})])],"derivedFrom":subQ2}),makeQuery(id+"F8.boolean.opBoolean","SPLIT",EDGE,{"disambiguationData":[TD([makeQuery(id+"F1.opExtrude","SWEPT_FACE",FACE,{"disambiguationData":[OSD([sQuery(id+"F0.wireOp",EDGE,"E0.bottom")])]})])],"derivedFrom":subQ2})]});}
            var Q1;
            {var subQ0=sQuery(id+"F2.wireOp",EDGE,"E13.top");var subQ1=sQuery(id+"F2.wireOp",EDGE,"E13.right");Q1=makeQuery(id+"F6.boolean.opBoolean","MERGE",EDGE,{"derivedFrom":[makeQuery(id+"F3.opExtrude","SWEPT_EDGE",EDGE,{"disambiguationData":[OSD([subQ0,subQ1])]}),makeQuery(id+"F6.opExtrude","SWEPT_EDGE",EDGE,{"disambiguationData":[OSD([subQ0,subQ1])]})]});}
            var Q2;
            {var subQ0=sQuery(id+"F2.wireOp",EDGE,"E15.top");var subQ1=sQuery(id+"F2.wireOp",EDGE,"E15.right");Q2=makeQuery(id+"F6.boolean.opBoolean","MERGE",EDGE,{"derivedFrom":[makeQuery(id+"F3.opExtrude","SWEPT_EDGE",EDGE,{"disambiguationData":[OSD([subQ0,subQ1])]}),makeQuery(id+"F6.opExtrude","SWEPT_EDGE",EDGE,{"disambiguationData":[OSD([subQ0,subQ1])]})]});}
            var Q3;
            {var subQ0=sQuery(id+"F2.wireOp",EDGE,"E15.bottom");var subQ1=sQuery(id+"F2.wireOp",EDGE,"E15.right");Q3=makeQuery(id+"F6.boolean.opBoolean","MERGE",EDGE,{"derivedFrom":[makeQuery(id+"F3.opExtrude","SWEPT_EDGE",EDGE,{"disambiguationData":[OSD([subQ0,subQ1])]}),makeQuery(id+"F6.opExtrude","SWEPT_EDGE",EDGE,{"disambiguationData":[OSD([subQ0,subQ1])]})]});}
            var Q4;
            {var subQ0=sQuery(id+"F2.wireOp",EDGE,"E14.top");var subQ1=sQuery(id+"F2.wireOp",EDGE,"E14.right");Q4=makeQuery(id+"F6.boolean.opBoolean","MERGE",EDGE,{"derivedFrom":[makeQuery(id+"F3.opExtrude","SWEPT_EDGE",EDGE,{"disambiguationData":[OSD([subQ0,subQ1])]}),makeQuery(id+"F6.opExtrude","SWEPT_EDGE",EDGE,{"disambiguationData":[OSD([subQ0,subQ1])]})]});}
            var Q5;
            {var subQ0=sQuery(id+"F2.wireOp",EDGE,"E14.bottom");var subQ1=sQuery(id+"F2.wireOp",EDGE,"E14.right");Q5=makeQuery(id+"F6.boolean.opBoolean","MERGE",EDGE,{"derivedFrom":[makeQuery(id+"F3.opExtrude","SWEPT_EDGE",EDGE,{"disambiguationData":[OSD([subQ0,subQ1])]}),makeQuery(id+"F6.opExtrude","SWEPT_EDGE",EDGE,{"disambiguationData":[OSD([subQ0,subQ1])]})]});}
            var Q6;
            {var subQ0=sQuery(id+"F2.wireOp",EDGE,"E12.bottom");var subQ1=sQuery(id+"F2.wireOp",EDGE,"E12.right");Q6=makeQuery(id+"F6.boolean.opBoolean","MERGE",EDGE,{"derivedFrom":[makeQuery(id+"F3.opExtrude","SWEPT_EDGE",EDGE,{"disambiguationData":[OSD([subQ0,subQ1])]}),makeQuery(id+"F6.opExtrude","SWEPT_EDGE",EDGE,{"disambiguationData":[OSD([subQ0,subQ1])]})]});}
            var Q7;
            {var subQ0=sQuery(id+"F2.wireOp",EDGE,"E12.top");var subQ1=sQuery(id+"F2.wireOp",EDGE,"E12.right");var subQ2=makeQuery(id+"F6.boolean.opBoolean","MERGE",EDGE,{"derivedFrom":[makeQuery(id+"F3.opExtrude","SWEPT_EDGE",EDGE,{"disambiguationData":[OSD([subQ0,subQ1])]}),makeQuery(id+"F6.opExtrude","SWEPT_EDGE",EDGE,{"disambiguationData":[OSD([subQ0,subQ1])]})]});var subQ5=sQuery(id+"F2.wireOp",EDGE,"E8.bottom");var subQ6=sQuery(id+"F2.wireOp",EDGE,"E8.top");var subQ7=sQuery(id+"F2.wireOp",EDGE,"E8.right");var subQ8=sQuery(id+"F2.wireOp",EDGE,"E10.bottom");var subQ9=sQuery(id+"F2.wireOp",EDGE,"E10.top");var subQ10=sQuery(id+"F2.wireOp",EDGE,"E10.right");var subQ11=sQuery(id+"F2.wireOp",EDGE,"E12.bottom");var subQ12=sQuery(id+"F2.wireOp",EDGE,"E13.bottom");var subQ13=sQuery(id+"F2.wireOp",EDGE,"E13.top");var subQ14=sQuery(id+"F2.wireOp",EDGE,"E13.right");Q7=makeQuery(id+"F9.opChamfer","MERGE",EDGE,{"derivedFrom":[makeQuery(id+"F8.boolean.opBoolean","SPLIT",EDGE,{"disambiguationData":[TD([makeQuery(id+"F6.opExtrude","CAP_FACE",FACE,{"disambiguationData":[OSD([sQuery(id+"F0.wireOp",EDGE,"E2"),subQ5,subQ6,subQ7,subQ8,subQ9,subQ10,subQ11,subQ0,subQ1,subQ12,subQ13,subQ14])],"isStart":false})])],"derivedFrom":subQ2}),makeQuery(id+"F8.boolean.opBoolean","SPLIT",EDGE,{"disambiguationData":[TD([makeQuery(id+"F1.opExtrude","SWEPT_FACE",FACE,{"disambiguationData":[OSD([sQuery(id+"F0.wireOp",EDGE,"E0.bottom")])]})])],"derivedFrom":subQ2})]});}
            var Q8;
            {var subQ0=sQuery(id+"F2.wireOp",EDGE,"E12.right");var subQ1=sQuery(id+"F2.wireOp",EDGE,"E8.top");var subQ2=sQuery(id+"F2.wireOp",EDGE,"E12.top");Q8=makeQuery(id+"F18.opFillet","TWEAK_EDGE",EDGE,{"derivedFrom":[makeQuery(id+"F9.opChamfer","BLEND_VERTEX",VERTEX,{"blendedFrom":[makeQuery(id+"F8.opExtrude","CAP_EDGE",EDGE,{"disambiguationData":[OSD([sQuery(id+"F7.wireOp",EDGE,"E21.left")])],"isStart":true}),makeQuery(id+"F6.boolean.opBoolean","MERGE",FACE,{"derivedFrom":[makeQuery(id+"F3.opExtrude","SWEPT_FACE",FACE,{"disambiguationData":[OSD([subQ0])]}),makeQuery(id+"F6.opExtrude","SWEPT_FACE",FACE,{"disambiguationData":[OSD([subQ0])]})]}),makeQuery(id+"F6.boolean.opBoolean","MERGE",FACE,{"derivedFrom":[makeQuery(id+"F3.opExtrude","SWEPT_FACE",FACE,{"disambiguationData":[OSD([subQ1,subQ2])]}),makeQuery(id+"F6.opExtrude","SWEPT_FACE",FACE,{"disambiguationData":[OSD([subQ1,subQ2])]})]}),makeQuery(id+"F8.opExtrude","SWEPT_FACE",FACE,{"disambiguationData":[OSD([sQuery(id+"F7.wireOp",EDGE,"E21.bottom")])]})],"blendedInto":[makeQuery(id+"F6.boolean.opBoolean","MERGE",FACE,{"derivedFrom":[makeQuery(id+"F3.opExtrude","SWEPT_FACE",FACE,{"disambiguationData":[OSD([subQ0])]}),makeQuery(id+"F6.opExtrude","SWEPT_FACE",FACE,{"disambiguationData":[OSD([subQ0])]})]}),makeQuery(id+"F6.boolean.opBoolean","MERGE",FACE,{"derivedFrom":[makeQuery(id+"F3.opExtrude","SWEPT_FACE",FACE,{"disambiguationData":[OSD([subQ1,subQ2])]}),makeQuery(id+"F6.opExtrude","SWEPT_FACE",FACE,{"disambiguationData":[OSD([subQ1,subQ2])]})]}),makeQuery(id+"F8.opExtrude","SWEPT_FACE",FACE,{"disambiguationData":[OSD([sQuery(id+"F7.wireOp",EDGE,"E21.bottom")])]})]})]});}
            var Q9;
            {var subQ0=sQuery(id+"F2.wireOp",EDGE,"E13.right");var subQ1=sQuery(id+"F2.wireOp",EDGE,"E10.bottom");var subQ2=sQuery(id+"F2.wireOp",EDGE,"E13.bottom");Q9=makeQuery(id+"F18.opFillet","TWEAK_EDGE",EDGE,{"derivedFrom":[makeQuery(id+"F9.opChamfer","BLEND_VERTEX",VERTEX,{"blendedFrom":[makeQuery(id+"F8.opExtrude","CAP_EDGE",EDGE,{"disambiguationData":[OSD([sQuery(id+"F7.wireOp",EDGE,"E21.left")])],"isStart":true}),makeQuery(id+"F6.boolean.opBoolean","MERGE",FACE,{"derivedFrom":[makeQuery(id+"F3.opExtrude","SWEPT_FACE",FACE,{"disambiguationData":[OSD([subQ0])]}),makeQuery(id+"F6.opExtrude","SWEPT_FACE",FACE,{"disambiguationData":[OSD([subQ0])]})]}),makeQuery(id+"F6.boolean.opBoolean","MERGE",FACE,{"derivedFrom":[makeQuery(id+"F3.opExtrude","SWEPT_FACE",FACE,{"disambiguationData":[OSD([subQ1,subQ2])]}),makeQuery(id+"F6.opExtrude","SWEPT_FACE",FACE,{"disambiguationData":[OSD([subQ1,subQ2])]})]}),makeQuery(id+"F8.opExtrude","SWEPT_FACE",FACE,{"disambiguationData":[OSD([sQuery(id+"F7.wireOp",EDGE,"E21.top")])]})],"blendedInto":[makeQuery(id+"F6.boolean.opBoolean","MERGE",FACE,{"derivedFrom":[makeQuery(id+"F3.opExtrude","SWEPT_FACE",FACE,{"disambiguationData":[OSD([subQ0])]}),makeQuery(id+"F6.opExtrude","SWEPT_FACE",FACE,{"disambiguationData":[OSD([subQ0])]})]}),makeQuery(id+"F6.boolean.opBoolean","MERGE",FACE,{"derivedFrom":[makeQuery(id+"F3.opExtrude","SWEPT_FACE",FACE,{"disambiguationData":[OSD([subQ1,subQ2])]}),makeQuery(id+"F6.opExtrude","SWEPT_FACE",FACE,{"disambiguationData":[OSD([subQ1,subQ2])]})]}),makeQuery(id+"F8.opExtrude","SWEPT_FACE",FACE,{"disambiguationData":[OSD([sQuery(id+"F7.wireOp",EDGE,"E21.top")])]})]})]});}
            fillet(context, id + "F19", {"entities" : qUnion([Q0, Q1, Q2, Q3, Q4, Q5, Q6, Q7, Q8, Q9]), "radius" : 7 * mm, "tangentPropagation" : true, "allowEdgeOverflow" : false});
        }
        {
            var Q0;
            Q0=makeQuery(id+"F3.boolean.opBoolean","MERGE",EDGE,{"derivedFrom":[makeQuery(id+"F1.opExtrude","CAP_EDGE",EDGE,{"disambiguationData":[OSD([sQuery(id+"F0.wireOp",EDGE,"E0.bottom")])],"isStart":true}),makeQuery(id+"F3.opExtrude","CAP_EDGE",EDGE,{"disambiguationData":[OSD([sQuery(id+"F2.wireOp",EDGE,"E8.bottom"),sQuery(id+"F2.wireOp",EDGE,"E12.bottom")])],"isStart":false}),makeQuery(id+"F3.opExtrude","CAP_EDGE",EDGE,{"disambiguationData":[OSD([sQuery(id+"F2.wireOp",EDGE,"E9.bottom"),sQuery(id+"F2.wireOp",EDGE,"E14.bottom")])],"isStart":false})]});
            var Q1;
            Q1=makeQuery(id+"F3.boolean.opBoolean","MERGE",EDGE,{"derivedFrom":[makeQuery(id+"F1.opExtrude","CAP_EDGE",EDGE,{"disambiguationData":[OSD([sQuery(id+"F0.wireOp",EDGE,"E0.bottom")])],"isStart":false}),makeQuery(id+"F3.opExtrude","CAP_EDGE",EDGE,{"disambiguationData":[OSD([sQuery(id+"F2.wireOp",EDGE,"E10.top"),sQuery(id+"F2.wireOp",EDGE,"E13.top")])],"isStart":false}),makeQuery(id+"F3.opExtrude","CAP_EDGE",EDGE,{"disambiguationData":[OSD([sQuery(id+"F2.wireOp",EDGE,"E11.top"),sQuery(id+"F2.wireOp",EDGE,"E15.top")])],"isStart":false})]});
            var Q2;
            Q2=makeQuery(id+"F8.opExtrude","CAP_EDGE",EDGE,{"disambiguationData":[OSD([sQuery(id+"F7.wireOp",EDGE,"E21.bottom")])],"isStart":false});
            var Q3;
            Q3=makeQuery(id+"F1.opExtrude","SWEPT_EDGE",EDGE,{"disambiguationData":[OSD([sQuery(id+"F0.wireOp",EDGE,"E0.bottom"),sQuery(id+"F0.wireOp",EDGE,"E0.right")])]});
            fillet(context, id + "F20", {"entities" : qUnion([Q0, Q1, Q2, Q3]), "radius" : 1 * mm, "tangentPropagation" : true, "allowEdgeOverflow" : false});
        }
    });
